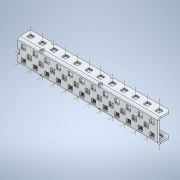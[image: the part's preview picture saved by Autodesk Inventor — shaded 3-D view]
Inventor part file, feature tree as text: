
AUTODESK INVENTOR PART (.ipt)
format: ipt  version: 2020 (Build 240168000, 168)  size: 1,262,592 bytes
history: native  units: in
note: dims shown in document units (in); Inventor stores cm internally (conversion verified against a paired STEP export)
features: other x63, plane x8, pattern_linear x4, split x2, sheet_metal_op x1
ambient origin geometry x8: Origin, YZ Plane, XZ Plane, XY Plane, X Axis, Y Axis, Z Axis, Center Point
bodies: Solid1 (feature_tree)
feature tree (78):
  other  "Work Axis1"
  pattern_linear  "Rectangular Pattern1"  Count1=12 Spacing1=0.5in
  other  "Work Axis72"
  pattern_linear  "Rectangular Pattern2"  Count1=12 Spacing1=0.5in
  pattern_linear  "Rectangular Pattern3"  Count1=12 Spacing1=0.5in
  other  "Work Axis141"
  pattern_linear  "Rectangular Pattern4"  Count1=11 Spacing1=0.5in
  plane  "Work Plane7"
  split  "Split1"
  plane  "Work Plane8"
  split  "Split2"
  plane  "Work Plane1"
  plane  "Work Plane2"
  other  "Work Point1"
  other  "Work Axis2"
  other  "Work Axis3"
  other  "Work Axis4"
  other  "Work Axis5"
  other  "Work Axis6"
  other  "Work Axis7"
  other  "Work Axis8"
  other  "Work Axis9"
  other  "Work Axis10"
  other  "Work Axis11"
  other  "Work Axis12"
  other  "Work Axis36"
  other  "Work Axis37"
  other  "Work Axis38"
  other  "Work Axis39"
  other  "Work Axis40"
  other  "Work Axis41"
  other  "Work Axis42"
  other  "Work Axis43"
  other  "Work Axis44"
  other  "Work Axis45"
  other  "Work Axis46"
  other  "Work Axis47"
  plane  "Work Plane3"
  plane  "Work Plane4"
  other  "Work Point2"
  other  "Work Axis71"
  other  "Work Point3"
  other  "Work Axis73"
  other  "Work Axis107"
  other  "Work Axis108"
  other  "Work Axis109"
  other  "Work Axis110"
  plane  "Work Plane5"
  plane  "Work Plane6"
  other  "Work Point4"
  other  "Work Axis142"
  other  "Work Axis143"
  other  "Work Axis144"
  other  "Work Axis145"
  other  "Work Axis146"
  other  "Work Axis147"
  other  "Work Axis148"
  other  "Work Axis149"
  other  "Work Axis150"
  other  "Work Axis151"
  other  "Work Axis175"
  other  "Work Axis176"
  other  "Work Axis177"
  other  "Work Axis178"
  other  "Work Axis179"
  other  "Work Axis180"
  other  "Work Axis181"
  other  "Work Axis185"
  other  "Work Axis186"
  other  "Work Axis187"
  other  "Work Axis188"
  other  "Work Axis189"
  other  "Work Axis190"
  other  "Work Axis191"
  other  "Work Axis192"
  other  "Work Axis193"
  other  "Work Axis194"
  sheet_metal_op  "Fold1"
